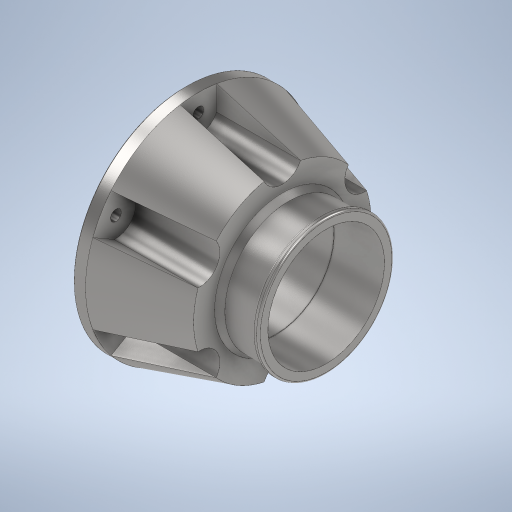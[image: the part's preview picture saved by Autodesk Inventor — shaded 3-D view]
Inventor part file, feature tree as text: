
AUTODESK INVENTOR PART (.ipt)
format: ipt  version: 2024 (Build 280153000, 153)  size: 445,440 bytes
history: native  units: mm
features: sketch x5, fillet x4, chamfer x4, hole x3, revolve x1, extrude x1, pattern_circular x1, projected_geometry x1
ambient origin geometry x8: Origin, YZ Plane, XZ Plane, XY Plane, X Axis, Y Axis, Z Axis, Center Point
bodies: Volumenkörper1 (feature_tree)
feature tree (20):
  revolve  "Umdrehung1"
  fillet  "Rundung1"  Radius=112.0mm
  fillet  "Rundung2"  Radius=2.792527mm
  fillet  "Rundung3"  Radius=108.0mm
  extrude  "Extrusion3"  Depth=102.0mm
  hole  "Bohrung3"  [1 undecoded]
  pattern_circular  "Runde Anordnung1"  [2 undecoded]
  chamfer  "Fasen1"  Distance=1.5mm
  chamfer  "Fasen3"  Distance=16.0mm
  hole  "Bohrung4"  [1 undecoded]
  hole  "Bohrung5"  [1 undecoded]
  chamfer  "Fasen4"  Distance=76.0mm
  chamfer  "Fasen5"  Distance=67.0mm
  fillet  "Rundung6"  Radius=3.0mm
  sketch  "Skizze1"  dims[d3=180.0mm d4=102.0mm]
  sketch  "Skizze2"  dims[d5=77.0mm d6=10.0mm]
  projected_geometry  "Projizierte Kontur1"
  sketch  "Skizze9"  dims[d7=5.0mm]
  sketch  "Skizze11"  dims[d8=90.0deg]
  sketch  "Skizze12"  dims[d9=1.2mm d10=1.5mm d11=1.5mm d16=16.0mm d19=60.0mm d20=360.0deg d46=1.0mm d47=2.0mm d48=45.0deg d54=76.0mm d55=67.0mm d56=0.0mm d57=8.5mm d58=6.0mm d59=4.0mm d60=2.0mm d61=90.0deg d62=8.0mm d63=20.594885mm d64=3.0mm d65=2.0mm d66=60.0deg d68=92.0mm d69=6.0mm d70=98.0mm d71=7.0mm d72=90.0deg d73=72.0mm d74=0.0mm d75=93.0mm d76=6.0mm d77=4.0mm d78=2.0mm d79=90.0deg d80=40.0mm d81=0.0mm d82=1.0mm d83=2.0mm d84=60.0deg d85=1.6mm d86=2.0mm d87=60.0deg d89=0.4mm]
note: 5 required parameter values undecoded (feature->parameter linkage not recoverable at this tier; creation-order binding heuristic only, values carry confidence <= 0.55)
